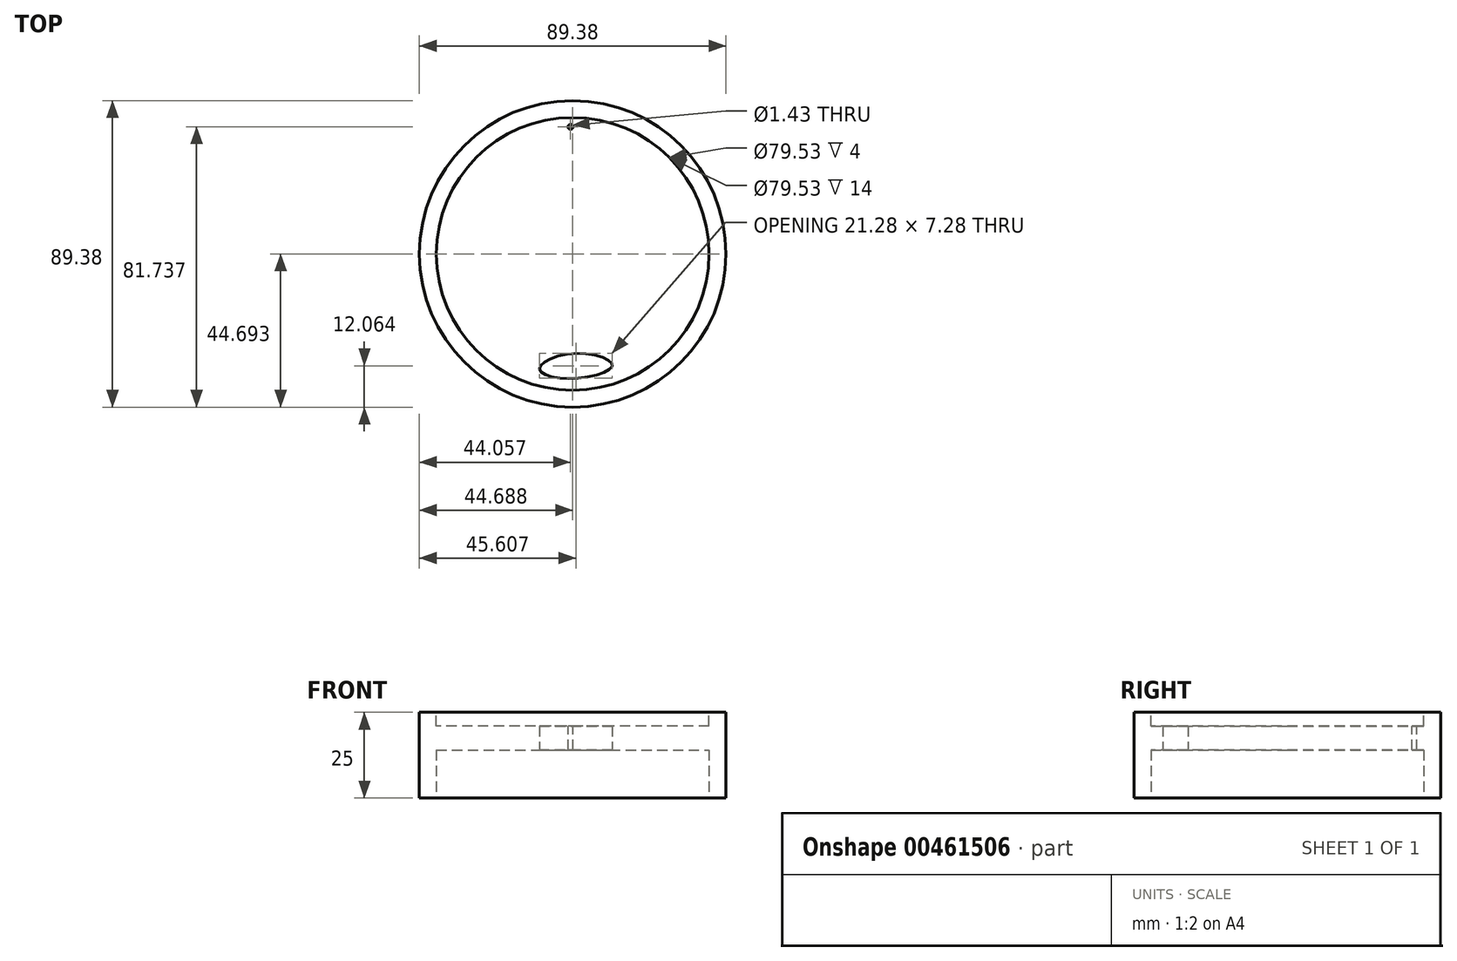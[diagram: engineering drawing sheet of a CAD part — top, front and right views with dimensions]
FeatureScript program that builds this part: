
annotation { "Feature Type Name" : "Feature", "Feature Type Description" : "" }
export const myFeature = defineFeature(function(context is Context, id is Id, definition is map)
    precondition{}
    {
        {
            var Q0;
            Q0=qCreatedBy(makeId("Top.planeOp"),FACE);
            var sketch = newSketch(context, id + "F0", { "sketchPlane" : qUnion([Q0])});
            skCircle(sketch, "E0", {"center": v(-15.16, 9.62) * mm, "radius": 44.7 * mm});
            skSolve(sketch);
        }
        {
            var Q0;
            Q0=makeQuery(id+"F0.imprint","IMPRINT",FACE,{"disambiguationData":[TD([[makeQuery(id+"F0.imprint","IMPRINT",EDGE,{"derivedFrom":sQuery(id+"F0.wireOp",EDGE,"E0")}),1.0]])]});
            extrude(context, id + "F1", {"entities" : qUnion([Q0]), "depth" : 25 * mm});
        }
        {
            var Q0;
            Q0=makeQuery(id+"F1.opExtrude","CAP_FACE",FACE,{"disambiguationData":[OSD([sQuery(id+"F0.wireOp",EDGE,"E0")])],"isStart":false});
            var sketch = newSketch(context, id + "F2", { "sketchPlane" : qUnion([Q0])});
            skCircle(sketch, "E1", {"center": v(-15.16, 9.62) * mm, "radius": 39.76 * mm});
            skSolve(sketch);
        }
        {
            var Q0;
            Q0=makeQuery(id+"F2.imprint","IMPRINT",FACE,{"disambiguationData":[TD([[makeQuery(id+"F2.imprint","IMPRINT",EDGE,{"derivedFrom":sQuery(id+"F2.wireOp",EDGE,"E1")}),1.0]])]});
            extrude(context, id + "F3", {"entities" : qUnion([Q0]), "operationType" : NewBodyOperationType.REMOVE, "oppositeDirection" : true, "depth" : 4 * mm});
        }
        {
            var Q0;
            Q0=makeQuery(id+"F3.boolean.opBoolean","COPY",FACE,{"derivedFrom":makeQuery(id+"F3.opExtrude","CAP_FACE",FACE,{"disambiguationData":[OSD([sQuery(id+"F2.wireOp",EDGE,"E1")])],"isStart":false})});
            var sketch = newSketch(context, id + "F4", { "sketchPlane" : qUnion([Q0])});
            skFitSpline(sketch, "E2", {"points": [v(-24.88, -23.98) * mm, v(-14.9, -26.68) * mm, v(-3.6, -22.79) * mm, v(-15.2, -19.39) * mm, v(-24.88, -23.98) * mm]});
            skSolve(sketch);
        }
        {
            var Q0;
            Q0=makeQuery(id+"F4.imprint","IMPRINT",FACE,{"disambiguationData":[TD([[makeQuery(id+"F4.imprint","IMPRINT",EDGE,{"derivedFrom":sQuery(id+"F4.wireOp",EDGE,"E2")}),1.0]])]});
            extrude(context, id + "F5", {"entities" : qUnion([Q0]), "operationType" : NewBodyOperationType.REMOVE, "endBound" : BoundingType.THROUGH_ALL, "oppositeDirection" : true, "depth" : 25 * mm});
        }
        {
            var Q0;
            Q0=makeQuery(id+"F3.boolean.opBoolean","COPY",FACE,{"derivedFrom":makeQuery(id+"F3.opExtrude","CAP_FACE",FACE,{"disambiguationData":[OSD([sQuery(id+"F2.wireOp",EDGE,"E1")])],"isStart":false})});
            var sketch = newSketch(context, id + "F6", { "sketchPlane" : qUnion([Q0])});
            skCircle(sketch, "E3", {"center": v(-15.8, 46.67) * mm, "radius": 0.72 * mm});
            skSolve(sketch);
        }
        {
            var Q0;
            Q0=makeQuery(id+"F6.imprint","IMPRINT",FACE,{"disambiguationData":[TD([[makeQuery(id+"F6.imprint","IMPRINT",EDGE,{"derivedFrom":sQuery(id+"F6.wireOp",EDGE,"E3")}),1.0]])]});
            extrude(context, id + "F7", {"entities" : qUnion([Q0]), "operationType" : NewBodyOperationType.REMOVE, "endBound" : BoundingType.THROUGH_ALL, "oppositeDirection" : true, "depth" : 25 * mm});
        }
        {
            var Q0;
            Q0=makeQuery(id+"F1.opExtrude","CAP_FACE",FACE,{"disambiguationData":[OSD([sQuery(id+"F0.wireOp",EDGE,"E0")])],"isStart":true});
            var sketch = newSketch(context, id + "F8", { "sketchPlane" : qUnion([Q0])});
            skCircle(sketch, "E4", {"center": v(-15.16, -9.62) * mm, "radius": 39.77 * mm});
            skSolve(sketch);
        }
        {
            var Q0;
            Q0=makeQuery(id+"F8.imprint","IMPRINT",FACE,{"disambiguationData":[TD([[makeQuery(id+"F8.imprint","IMPRINT",EDGE,{"derivedFrom":sQuery(id+"F8.wireOp",EDGE,"E4")}),1.0]])]});
            extrude(context, id + "F9", {"entities" : qUnion([Q0]), "operationType" : NewBodyOperationType.REMOVE, "oppositeDirection" : true, "depth" : 14 * mm});
        }
    });
